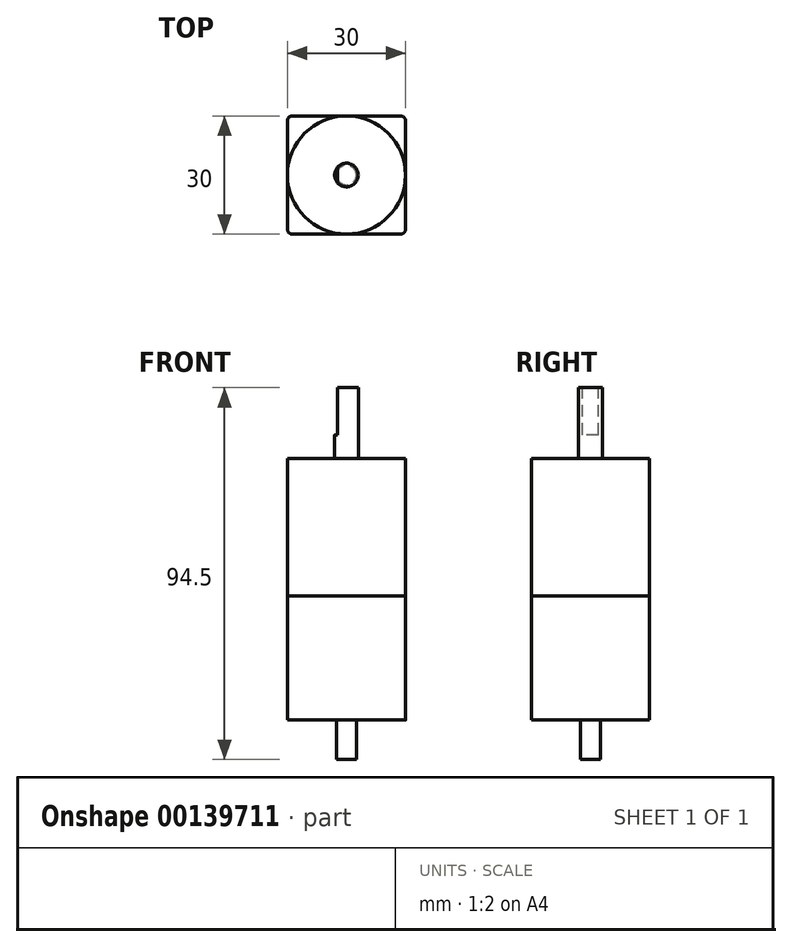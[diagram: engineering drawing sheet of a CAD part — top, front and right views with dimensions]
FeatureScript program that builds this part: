
annotation { "Feature Type Name" : "Feature", "Feature Type Description" : "" }
export const myFeature = defineFeature(function(context is Context, id is Id, definition is map)
    precondition{}
    {
        {
            assignVariable(context, id + "F0", {"name" : "MotorL", "anyValue" : 31.5});
        }
        {
            assignVariable(context, id + "F1", {"name" : "GearboxL", "anyValue" : 35});
        }
        {
            assignVariable(context, id + "F2", {"name" : "FrontShaftL", "anyValue" : 18});
        }
        {
            assignVariable(context, id + "F3", {"name" : "FrontShaftDCutL", "anyValue" : 12});
        }
        {
            assignVariable(context, id + "F4", {"name" : "RearShaftL", "anyValue" : 10});
        }
        {
            var Q0;
            Q0=qCreatedBy(makeId("Top.planeOp"),FACE);
            var sketch = newSketch(context, id + "F5", { "sketchPlane" : qUnion([Q0])});
            skLineSegment(sketch, "E0.bottom", {"start": v(-15, 15) * mm, "end": v(15, 15) * mm});
            skLineSegment(sketch, "E0.top", {"start": v(-15, -15) * mm, "end": v(15, -15) * mm});
            skLineSegment(sketch, "E0.left", {"start": v(-15, 15) * mm, "end": v(-15, -15) * mm});
            skLineSegment(sketch, "E0.right", {"start": v(15, 15) * mm, "end": v(15, -15) * mm});
            skSolve(sketch);
        }
        {
            var Q0;
            Q0=makeQuery(id+"F5.imprint","IMPRINT",FACE,{"disambiguationData":[TD([[makeQuery(id+"F5.imprint","IMPRINT",EDGE,{"derivedFrom":sQuery(id+"F5.wireOp",EDGE,"E0.bottom")}),-1.0]])]});
            extrude(context, id + "F6", {"entities" : qUnion([Q0]), "depth" : (getVariable(context, 'MotorL')) * mm});
        }
        {
            var Q0;
            Q0=makeQuery(id+"F6.opExtrude","CAP_FACE",FACE,{"disambiguationData":[OSD([sQuery(id+"F5.wireOp",EDGE,"E0.bottom"),sQuery(id+"F5.wireOp",EDGE,"E0.top"),sQuery(id+"F5.wireOp",EDGE,"E0.left"),sQuery(id+"F5.wireOp",EDGE,"E0.right")])],"isStart":false});
            var sketch = newSketch(context, id + "F7", { "sketchPlane" : qUnion([Q0])});
            skCircle(sketch, "E1", {"center": v(0, 0) * mm, "radius": 15 * mm});
            skSolve(sketch);
        }
        {
            var Q0;
            Q0=qSketchRegion(id+"F7",true);
            extrude(context, id + "F8", {"entities" : qUnion([Q0]), "depth" : (getVariable(context, 'GearboxL')) * mm});
        }
        {
            var Q0;
            Q0=makeQuery(id+"F8.opExtrude","CAP_FACE",FACE,{"disambiguationData":[OSD([sQuery(id+"F7.wireOp",EDGE,"E1")])],"isStart":false});
            var sketch = newSketch(context, id + "F9", { "sketchPlane" : qUnion([Q0])});
            skCircle(sketch, "E2", {"center": v(0, 0) * mm, "radius": 3 * mm});
            skSolve(sketch);
        }
        {
            var Q0;
            Q0=qSketchRegion(id+"F9",true);
            extrude(context, id + "F10", {"entities" : qUnion([Q0]), "operationType" : NewBodyOperationType.ADD, "depth" : (getVariable(context, 'FrontShaftL')) * mm});
        }
        {
            var Q0;
            Q0=makeQuery(id+"F10.opExtrude","CAP_FACE",FACE,{"disambiguationData":[OSD([sQuery(id+"F9.wireOp",EDGE,"E2")])],"isStart":false});
            var sketch = newSketch(context, id + "F11", { "sketchPlane" : qUnion([Q0])});
            skLineSegment(sketch, "E3", {"start": v(-2.25, 1.98) * mm, "end": v(-2.25, -1.98) * mm});
            skSolve(sketch);
        }
        {
            var Q0;
            {var subQ0=sQuery(id+"F11.wireOp",EDGE,"E3");Q0=makeQuery(id+"F11.imprint","IMPRINT",FACE,{"disambiguationData":[TD([[makeQuery(id+"F11.imprint","IMPRINT",EDGE,{"derivedFrom":subQ0}),-1.0]])]});}
            extrude(context, id + "F12", {"entities" : qUnion([Q0]), "operationType" : NewBodyOperationType.REMOVE, "oppositeDirection" : true, "depth" : (getVariable(context, 'FrontShaftDCutL')) * mm});
        }
        {
            var Q0;
            Q0=makeQuery(id+"F6.opExtrude","CAP_FACE",FACE,{"disambiguationData":[OSD([sQuery(id+"F5.wireOp",EDGE,"E0.bottom"),sQuery(id+"F5.wireOp",EDGE,"E0.top"),sQuery(id+"F5.wireOp",EDGE,"E0.left"),sQuery(id+"F5.wireOp",EDGE,"E0.right")])],"isStart":true});
            var sketch = newSketch(context, id + "F13", { "sketchPlane" : qUnion([Q0])});
            skCircle(sketch, "E4", {"center": v(0, 0) * mm, "radius": 2.5 * mm});
            skSolve(sketch);
        }
        {
            var Q0;
            Q0=qSketchRegion(id+"F13",true);
            extrude(context, id + "F14", {"entities" : qUnion([Q0]), "operationType" : NewBodyOperationType.ADD, "depth" : (getVariable(context, 'RearShaftL')) * mm});
        }
        {
            var Q0;
            Q0=makeQuery(id+"F6.opExtrude","SWEPT_EDGE",EDGE,{"disambiguationData":[OSD([sQuery(id+"F5.wireOp",EDGE,"E0.top"),sQuery(id+"F5.wireOp",EDGE,"E0.left")])]});
            var Q1;
            Q1=makeQuery(id+"F6.opExtrude","SWEPT_EDGE",EDGE,{"disambiguationData":[OSD([sQuery(id+"F5.wireOp",EDGE,"E0.top"),sQuery(id+"F5.wireOp",EDGE,"E0.right")])]});
            var Q2;
            Q2=makeQuery(id+"F6.opExtrude","SWEPT_EDGE",EDGE,{"disambiguationData":[OSD([sQuery(id+"F5.wireOp",EDGE,"E0.bottom"),sQuery(id+"F5.wireOp",EDGE,"E0.right")])]});
            var Q3;
            Q3=makeQuery(id+"F6.opExtrude","SWEPT_EDGE",EDGE,{"disambiguationData":[OSD([sQuery(id+"F5.wireOp",EDGE,"E0.bottom"),sQuery(id+"F5.wireOp",EDGE,"E0.left")])]});
            fillet(context, id + "F15", {"entities" : qUnion([Q0, Q1, Q2, Q3]), "radius" : 1.2 * mm, "tangentPropagation" : true, "allowEdgeOverflow" : false});
        }
    });
